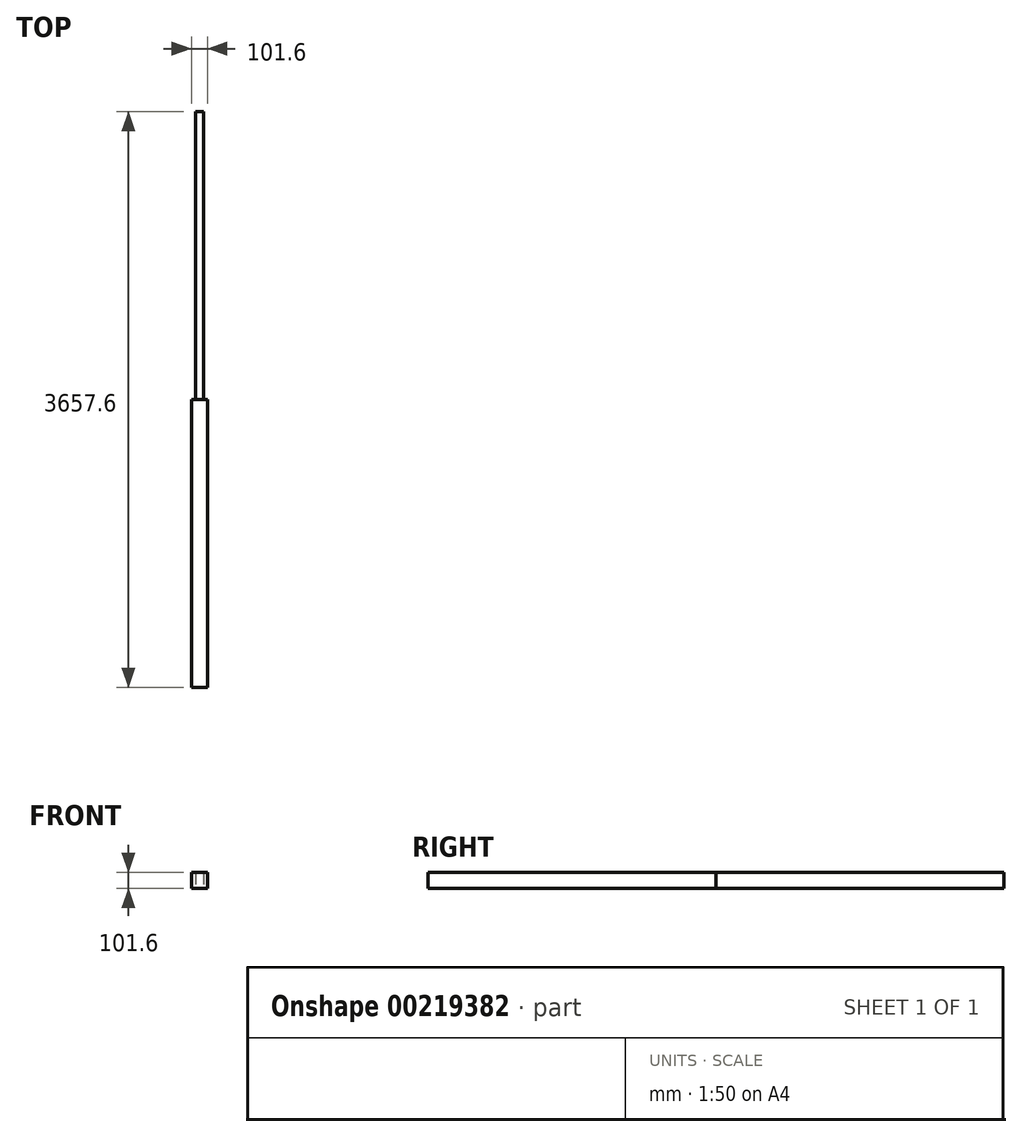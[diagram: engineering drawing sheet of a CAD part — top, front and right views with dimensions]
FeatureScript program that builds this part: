
annotation { "Feature Type Name" : "Feature", "Feature Type Description" : "" }
export const myFeature = defineFeature(function(context is Context, id is Id, definition is map)
    precondition{}
    {
        {
            var Q0;
            Q0=qCreatedBy(makeId("Right.planeOp"),FACE);
            var sketch = newSketch(context, id + "F0", { "sketchPlane" : qUnion([Q0])});
            skLineSegment(sketch, "E0.bottom", {"start": v(-1795.03, -326.28) * mm, "end": v(33.77, -326.28) * mm});
            skLineSegment(sketch, "E0.top", {"start": v(-1795.03, -224.68) * mm, "end": v(33.77, -224.68) * mm});
            skLineSegment(sketch, "E0.left", {"start": v(-1795.03, -326.28) * mm, "end": v(-1795.03, -224.68) * mm});
            skLineSegment(sketch, "E0.right", {"start": v(33.77, -326.28) * mm, "end": v(33.77, -224.68) * mm});
            skSolve(sketch);
        }
        {
            var Q0;
            Q0 = qSketchRegion(id + "F0", true);
            extrude(context, id + "F1", {"entities" : qUnion([Q0]), "depth" : 101.6 * mm});
        }
        {
            var Q0;
            Q0=makeQuery(id+"F1.opExtrude","SWEPT_FACE",FACE,{"disambiguationData":[OSD([sQuery(id+"F0.wireOp",EDGE,"E0.right")])]});
            var sketch = newSketch(context, id + "F2", { "sketchPlane" : qUnion([Q0])});
            skLineSegment(sketch, "E1", {"start": v(-50.8, -224.68) * mm, "end": v(-50.8, -326.28) * mm});
            skLineSegment(sketch, "E2", {"start": v(-25.4, -224.68) * mm, "end": v(-25.4, -326.28) * mm});
            skLineSegment(sketch, "E3.MirrorCS", {"start": v(-76.2, -224.68) * mm, "end": v(-76.2, -326.28) * mm});
            skSolve(sketch);
        }
        {
            var Q0;
            {var subQ0=sQuery(id+"F2.wireOp",EDGE,"E1");Q0=makeQuery(id+"F2.imprint","IMPRINT",FACE,{"disambiguationData":[TD([[makeQuery(id+"F2.imprint","IMPRINT",EDGE,{"derivedFrom":subQ0}),-1.0]])]});}
            var Q1;
            {var subQ0=sQuery(id+"F2.wireOp",EDGE,"E1");Q1=makeQuery(id+"F2.imprint","IMPRINT",FACE,{"disambiguationData":[TD([[makeQuery(id+"F2.imprint","IMPRINT",EDGE,{"derivedFrom":subQ0}),1.0]])]});}
            extrude(context, id + "F3", {"entities" : qUnion([Q0, Q1]), "depth" : 1828.8 * mm});
        }
    });
